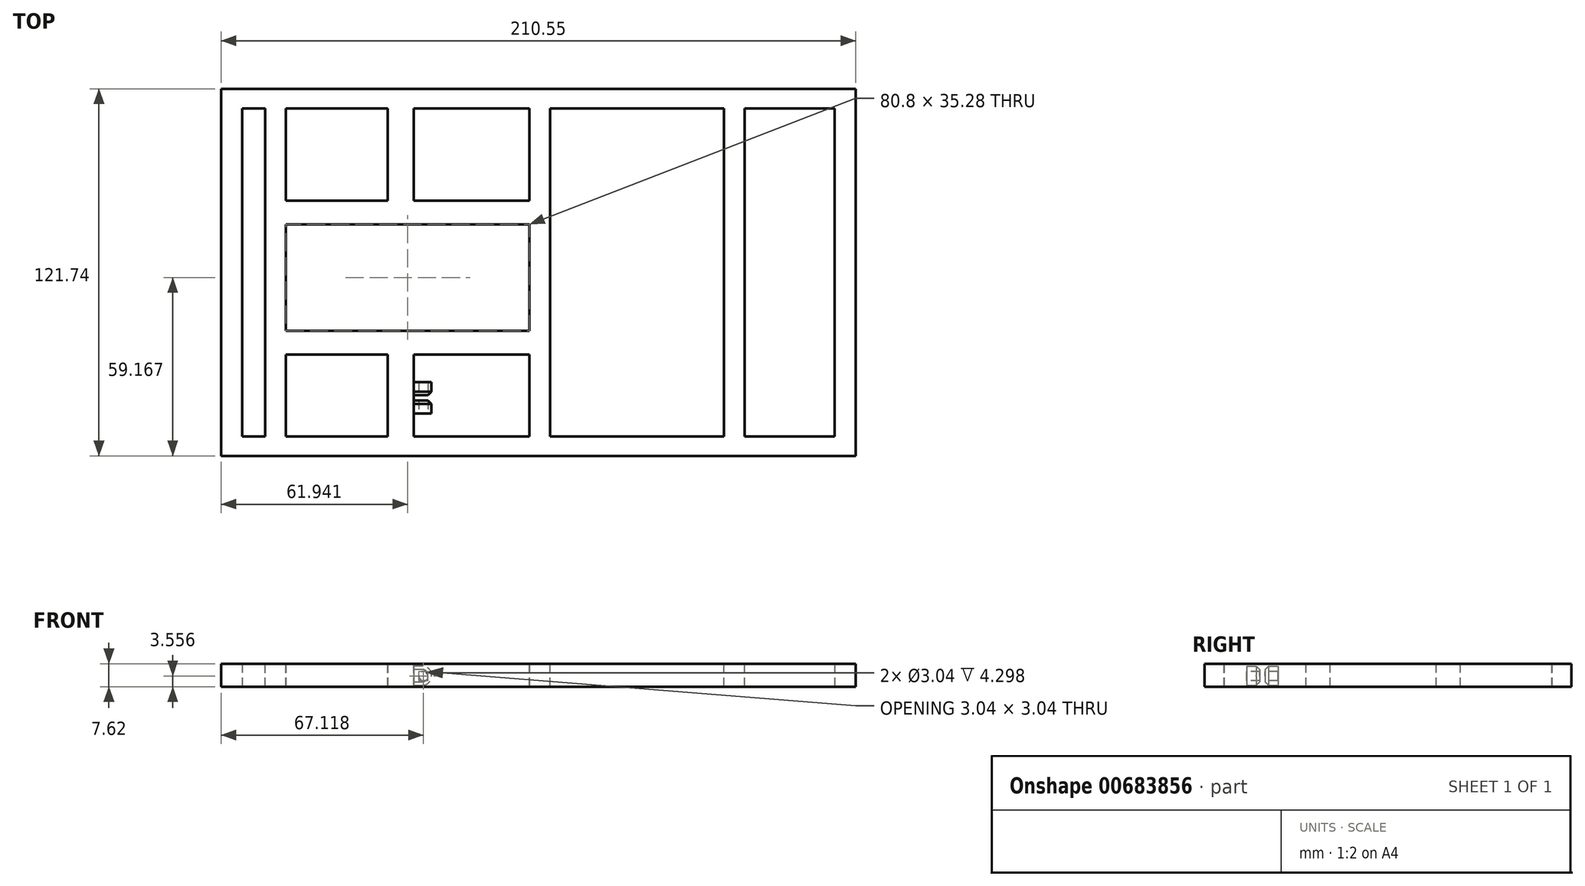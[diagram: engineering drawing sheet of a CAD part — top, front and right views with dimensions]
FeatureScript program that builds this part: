
annotation { "Feature Type Name" : "Feature", "Feature Type Description" : "" }
export const myFeature = defineFeature(function(context is Context, id is Id, definition is map)
    precondition{}
    {
        {
            var Q0;
            Q0=qCreatedBy(makeId("Top.planeOp"),FACE);
            var sketch = newSketch(context, id + "F0", { "sketchPlane" : qUnion([Q0])});
            skLineSegment(sketch, "E0.bottom", {"start": v(117.36, -60.87) * mm, "end": v(-93.2, -60.87) * mm});
            skLineSegment(sketch, "E0.top", {"start": v(117.36, 60.87) * mm, "end": v(-93.2, 60.87) * mm});
            skLineSegment(sketch, "E0.left", {"start": v(117.36, -60.87) * mm, "end": v(117.36, 60.87) * mm});
            skLineSegment(sketch, "E0.right", {"start": v(-117.36, -60.87) * mm, "end": v(-117.36, 60.87) * mm});
            skPoint(sketch, "E0.middle", {"position": v(0, 0) * mm});
            skLineSegment(sketch, "E1", {"start": v(-110.35, 50.5) * mm, "end": v(-110.35, -50.5) * mm});
            skLineSegment(sketch, "E2.MirrorCS", {"start": v(110.35, 50.5) * mm, "end": v(110.35, -50.5) * mm});
            skLineSegment(sketch, "E3", {"start": v(-110.35, 50.5) * mm, "end": v(-110.35, 54.4) * mm});
            skLineSegment(sketch, "E4", {"start": v(-93.2, 54.4) * mm, "end": v(110.35, 54.4) * mm});
            skLineSegment(sketch, "E5", {"start": v(110.35, 50.5) * mm, "end": v(110.35, 54.4) * mm});
            skPoint(sketch, "E6.orphan", {"position": v(113.1, 54.4) * mm});
            skLineSegment(sketch, "E7.MirrorCS", {"start": v(-93.2, -54.4) * mm, "end": v(110.35, -54.4) * mm});
            skLineSegment(sketch, "E8", {"start": v(-110.35, -50.5) * mm, "end": v(-110.35, -54.4) * mm});
            skLineSegment(sketch, "E9", {"start": v(110.35, -50.5) * mm, "end": v(110.35, -54.4) * mm});
            skLineSegment(sketch, "E10", {"start": v(-86.08, -54.4) * mm, "end": v(-86.08, 54.4) * mm});
            skLineSegment(sketch, "E11", {"start": v(-93.2, -60.87) * mm, "end": v(-93.2, 60.87) * mm});
            skSolve(sketch);
        }
        {
            var Q0;
            Q0=makeQuery(id+"F0.imprint","IMPRINT",FACE,{"disambiguationData":[TD([[makeQuery(id+"F0.imprint","IMPRINT",EDGE,{"derivedFrom":sQuery(id+"F0.wireOp",EDGE,"E0.bottom")}),-1.0]])]});
            var Q1;
            {var subQ3=sQuery(id+"F0.wireOp",EDGE,"E10");Q1=makeQuery(id+"F0.imprint","IMPRINT",FACE,{"disambiguationData":[TD([[makeQuery(id+"F0.imprint","IMPRINT",EDGE,{"derivedFrom":subQ3}),1.0]])]});}
            extrude(context, id + "F1", {"entities" : qUnion([Q0, Q1]), "depth" : 7.62 * mm, "offsetDistance" : 25.4 * mm});
        }
        {
            var Q0;
            Q0=makeQuery(id+"F1.opExtrude","CAP_FACE",FACE,{"disambiguationData":[OSD([sQuery(id+"F0.wireOp",EDGE,"E0.bottom"),sQuery(id+"F0.wireOp",EDGE,"E0.top"),sQuery(id+"F0.wireOp",EDGE,"E0.left"),sQuery(id+"F0.wireOp",EDGE,"E0.right"),sQuery(id+"F0.wireOp",EDGE,"E1"),sQuery(id+"F0.wireOp",EDGE,"E2.MirrorCS"),sQuery(id+"F0.wireOp",EDGE,"E3"),sQuery(id+"F0.wireOp",EDGE,"E4"),sQuery(id+"F0.wireOp",EDGE,"E5"),sQuery(id+"F0.wireOp",EDGE,"E7.MirrorCS"),sQuery(id+"F0.wireOp",EDGE,"E8"),sQuery(id+"F0.wireOp",EDGE,"E9")])],"isStart":true});
            var sketch = newSketch(context, id + "F2", { "sketchPlane" : qUnion([Q0])});
            skLineSegment(sketch, "E12.bottom", {"start": v(80.5, 60.87) * mm, "end": v(73.64, 60.87) * mm});
            skLineSegment(sketch, "E12.top", {"start": v(80.5, -60.87) * mm, "end": v(73.64, -60.87) * mm});
            skLineSegment(sketch, "E12.left", {"start": v(80.5, 60.87) * mm, "end": v(80.5, -60.87) * mm});
            skLineSegment(sketch, "E12.right", {"start": v(73.64, 60.87) * mm, "end": v(73.64, -60.87) * mm});
            skLineSegment(sketch, "E13.bottom", {"start": v(-71.65, 60.87) * mm, "end": v(-78.5, 60.87) * mm});
            skLineSegment(sketch, "E13.top", {"start": v(-71.65, -60.87) * mm, "end": v(-78.5, -60.87) * mm});
            skLineSegment(sketch, "E13.left", {"start": v(-71.65, 60.87) * mm, "end": v(-71.65, -60.87) * mm});
            skLineSegment(sketch, "E13.right", {"start": v(-78.5, 60.87) * mm, "end": v(-78.5, -60.87) * mm});
            skLineSegment(sketch, "E14.bottom", {"start": v(16.01, 60.87) * mm, "end": v(9.15, 60.87) * mm});
            skLineSegment(sketch, "E14.top", {"start": v(16.01, -60.87) * mm, "end": v(9.15, -60.87) * mm});
            skLineSegment(sketch, "E14.left", {"start": v(16.01, 60.87) * mm, "end": v(16.01, -60.87) * mm});
            skLineSegment(sketch, "E14.right", {"start": v(9.15, 60.87) * mm, "end": v(9.15, -60.87) * mm});
            skLineSegment(sketch, "E15", {"start": v(-78.5, -15.94) * mm, "end": v(-78.5, -23.83) * mm});
            skLineSegment(sketch, "E16", {"start": v(-78.5, 27.25) * mm, "end": v(-78.5, 19.34) * mm});
            skLineSegment(sketch, "E17.bottom", {"start": v(-37.85, 60.87) * mm, "end": v(-29.19, 60.87) * mm});
            skLineSegment(sketch, "E17.top", {"start": v(-37.85, -60.87) * mm, "end": v(-29.19, -60.87) * mm});
            skLineSegment(sketch, "E17.left", {"start": v(-37.85, 60.87) * mm, "end": v(-37.85, -60.87) * mm});
            skLineSegment(sketch, "E17.right", {"start": v(-29.19, 60.87) * mm, "end": v(-29.19, -60.87) * mm});
            skLineSegment(sketch, "E18.bottom", {"start": v(-78.5, 27.25) * mm, "end": v(16.01, 27.25) * mm});
            skLineSegment(sketch, "E18.top", {"start": v(-78.5, 19.34) * mm, "end": v(16.01, 19.34) * mm});
            skLineSegment(sketch, "E18.right", {"start": v(16.01, 27.25) * mm, "end": v(16.01, 19.34) * mm});
            skLineSegment(sketch, "E19.bottom", {"start": v(-78.5, -15.94) * mm, "end": v(16.01, -15.94) * mm});
            skLineSegment(sketch, "E19.top", {"start": v(-78.5, -23.83) * mm, "end": v(16.01, -23.83) * mm});
            skLineSegment(sketch, "E19.right", {"start": v(16.01, -15.94) * mm, "end": v(16.01, -23.83) * mm});
            skSolve(sketch);
        }
        {
            var Q0;
            Q0 = qSketchRegion(id + "F2", true);
            extrude(context, id + "F3", {"entities" : qUnion([Q0]), "operationType" : NewBodyOperationType.ADD, "oppositeDirection" : true, "depth" : 7.62 * mm, "offsetDistance" : 25.4 * mm});
        }
        {
            var Q0;
            {var subQ0=sQuery(id+"F2.wireOp",EDGE,"E17.right");var subQ1=makeQuery(id+"F2.imprint","INTERSECT",VERTEX,{"derivedFrom":[makeQuery(id+"F1.opExtrude","CAP_EDGE",EDGE,{"disambiguationData":[OSD([sQuery(id+"F0.wireOp",EDGE,"E7.MirrorCS")])],"isStart":true}),subQ0]});Q0=makeQuery(id+"F3.opExtrude","SWEPT_FACE",FACE,{"disambiguationData":[OSD([subQ0]),TDD([makeQuery(id+"F2.imprint","IMPRINT",EDGE,{"disambiguationData":[TD([[subQ1,1.0]])],"derivedFrom":subQ0}),makeQuery(id+"F2.imprint","IMPRINT",EDGE,{"disambiguationData":[TD([[makeQuery(id+"F2.imprint","INTERSECT",VERTEX,{"derivedFrom":[sQuery(id+"F2.wireOp",EDGE,"RkB2jaZS-KFBK-mtPf-oNwH-4hhG9Da7ueCo.bottom"),subQ0]}),1.0]])],"derivedFrom":subQ0})])]});}
            var sketch = newSketch(context, id + "F4", { "sketchPlane" : qUnion([Q0])});
            skLineSegment(sketch, "E20.bottom", {"start": v(-46.79, 6.87) * mm, "end": v(-36.42, 6.87) * mm});
            skLineSegment(sketch, "E20.top", {"start": v(-46.79, 0.5) * mm, "end": v(-36.42, 0.5) * mm});
            skLineSegment(sketch, "E20.left", {"start": v(-46.79, 6.87) * mm, "end": v(-46.79, 0.5) * mm});
            skLineSegment(sketch, "E20.right", {"start": v(-36.42, 6.87) * mm, "end": v(-36.42, 0.5) * mm});
            skSolve(sketch);
        }
        {
            var Q0;
            Q0=makeQuery(id+"F4.imprint","IMPRINT",FACE,{"disambiguationData":[TD([[makeQuery(id+"F4.imprint","IMPRINT",EDGE,{"derivedFrom":sQuery(id+"F4.wireOp",EDGE,"E20.bottom")}),-1.0]])]});
            extrude(context, id + "F5", {"entities" : qUnion([Q0]), "operationType" : NewBodyOperationType.ADD, "depth" : 5.84 * mm, "offsetDistance" : 25.4 * mm});
        }
        {
            var Q0;
            Q0=makeQuery(id+"F5.opExtrude","CAP_EDGE",EDGE,{"disambiguationData":[OSD([sQuery(id+"F4.wireOp",EDGE,"E20.top")])],"isStart":false});
            var Q1;
            Q1=makeQuery(id+"F5.opExtrude","CAP_EDGE",EDGE,{"disambiguationData":[OSD([sQuery(id+"F4.wireOp",EDGE,"E20.bottom")])],"isStart":false});
            fillet(context, id + "F6", {"entities" : qUnion([Q0, Q1]), "radius" : 3.05 * mm, "tangentPropagation" : true, "allowEdgeOverflow" : false});
        }
        {
            var Q0;
            Q0=makeQuery(id+"F5.opExtrude","SWEPT_FACE",FACE,{"disambiguationData":[OSD([sQuery(id+"F4.wireOp",EDGE,"E20.left")])]});
            var sketch = newSketch(context, id + "F7", { "sketchPlane" : qUnion([Q0])});
            skCircle(sketch, "E21", {"center": v(-26.07, 3.56) * mm, "radius": 1.52 * mm});
            skPoint(sketch, "E22", {"position": v(-29.19, 3.7) * mm});
            skSolve(sketch);
        }
        {
            var Q0;
            Q0=makeQuery(id+"F7.imprint","IMPRINT",FACE,{"disambiguationData":[TD([[makeQuery(id+"F7.imprint","IMPRINT",EDGE,{"derivedFrom":sQuery(id+"F7.wireOp",EDGE,"E21")}),1.0]])]});
            extrude(context, id + "F8", {"entities" : qUnion([Q0]), "operationType" : NewBodyOperationType.REMOVE, "oppositeDirection" : true, "depth" : 10.36 * mm, "offsetDistance" : 25.4 * mm});
        }
        {
            var Q0;
            {var subQ0=sQuery(id+"F2.wireOp",EDGE,"E17.right");var subQ1=makeQuery(id+"F2.imprint","INTERSECT",VERTEX,{"derivedFrom":[makeQuery(id+"F1.opExtrude","CAP_EDGE",EDGE,{"disambiguationData":[OSD([sQuery(id+"F0.wireOp",EDGE,"E7.MirrorCS")])],"isStart":true}),subQ0]});Q0=makeQuery(id+"F3.opExtrude","SWEPT_FACE",FACE,{"disambiguationData":[OSD([subQ0]),TDD([makeQuery(id+"F2.imprint","IMPRINT",EDGE,{"disambiguationData":[TD([[subQ1,1.0]])],"derivedFrom":subQ0}),makeQuery(id+"F2.imprint","IMPRINT",EDGE,{"disambiguationData":[TD([[makeQuery(id+"F2.imprint","INTERSECT",VERTEX,{"derivedFrom":[sQuery(id+"F2.wireOp",EDGE,"RkB2jaZS-KFBK-mtPf-oNwH-4hhG9Da7ueCo.bottom"),subQ0]}),1.0]])],"derivedFrom":subQ0})])]});}
            var sketch = newSketch(context, id + "F9", { "sketchPlane" : qUnion([Q0])});
            skLineSegment(sketch, "E23.bottom", {"start": v(-42.49, 6.87) * mm, "end": v(-40.72, 6.87) * mm});
            skLineSegment(sketch, "E23.top", {"start": v(-42.49, -0.41) * mm, "end": v(-40.72, -0.41) * mm});
            skLineSegment(sketch, "E23.left", {"start": v(-42.49, 6.87) * mm, "end": v(-42.49, -0.41) * mm});
            skLineSegment(sketch, "E23.right", {"start": v(-40.72, 6.87) * mm, "end": v(-40.72, -0.41) * mm});
            skSolve(sketch);
        }
        {
            var Q0;
            Q0=qSketchRegion(id+"F9",true);
            extrude(context, id + "F10", {"entities" : qUnion([Q0]), "operationType" : NewBodyOperationType.REMOVE, "depth" : 5.84 * mm, "offsetDistance" : 25.4 * mm});
        }
        {
            var Q0;
            Q0=makeQuery(id+"F10.boolean.opBoolean","INTERSECT",EDGE,{"derivedFrom":[makeQuery(id+"F6.opFillet","BLEND_FACE",FACE,{"disambiguationData":[OSD([sQuery(id+"F4.wireOp",EDGE,"E20.top")])]}),makeQuery(id+"F10.opExtrude","SWEPT_FACE",FACE,{"disambiguationData":[OSD([sQuery(id+"F9.wireOp",EDGE,"E23.left")])]})]});
            var Q1;
            Q1=makeQuery(id+"F10.boolean.opBoolean","COPY",EDGE,{"derivedFrom":makeQuery(id+"F10.opExtrude","CAP_EDGE",EDGE,{"disambiguationData":[OSD([sQuery(id+"F9.wireOp",EDGE,"E23.left")])],"isStart":false})});
            var Q2;
            Q2=makeQuery(id+"F10.boolean.opBoolean","INTERSECT",EDGE,{"derivedFrom":[makeQuery(id+"F6.opFillet","BLEND_FACE",FACE,{"disambiguationData":[OSD([sQuery(id+"F4.wireOp",EDGE,"E20.bottom")])]}),makeQuery(id+"F10.opExtrude","SWEPT_FACE",FACE,{"disambiguationData":[OSD([sQuery(id+"F9.wireOp",EDGE,"E23.left")])]})]});
            var Q3;
            Q3=makeQuery(id+"F10.boolean.opBoolean","COPY",EDGE,{"derivedFrom":makeQuery(id+"F10.opExtrude","CAP_EDGE",EDGE,{"disambiguationData":[OSD([sQuery(id+"F9.wireOp",EDGE,"E23.right")])],"isStart":false})});
            var Q4;
            Q4=makeQuery(id+"F10.boolean.opBoolean","INTERSECT",EDGE,{"derivedFrom":[makeQuery(id+"F6.opFillet","BLEND_FACE",FACE,{"disambiguationData":[OSD([sQuery(id+"F4.wireOp",EDGE,"E20.bottom")])]}),makeQuery(id+"F10.opExtrude","SWEPT_FACE",FACE,{"disambiguationData":[OSD([sQuery(id+"F9.wireOp",EDGE,"E23.right")])]})]});
            var Q5;
            Q5=makeQuery(id+"F10.boolean.opBoolean","INTERSECT",EDGE,{"derivedFrom":[makeQuery(id+"F6.opFillet","BLEND_FACE",FACE,{"disambiguationData":[OSD([sQuery(id+"F4.wireOp",EDGE,"E20.top")])]}),makeQuery(id+"F10.opExtrude","SWEPT_FACE",FACE,{"disambiguationData":[OSD([sQuery(id+"F9.wireOp",EDGE,"E23.right")])]})]});
            chamfer(context, id + "F11", {"entities" : qUnion([Q0, Q1, Q2, Q3, Q4, Q5]), "width" : 1.14 * mm, "tangentPropagation" : true});
        }
    });
